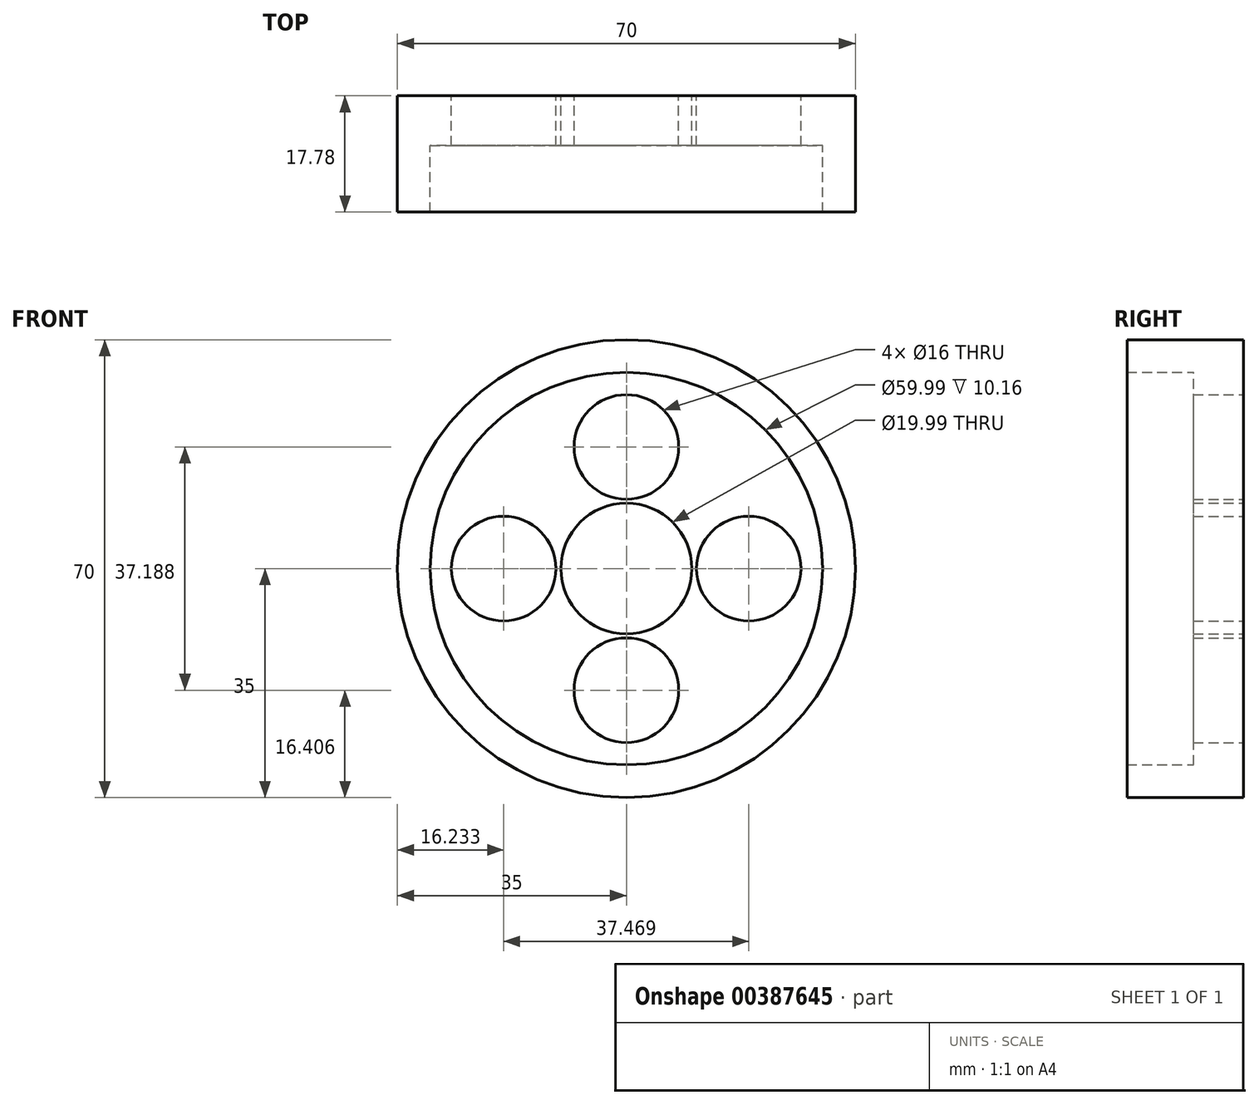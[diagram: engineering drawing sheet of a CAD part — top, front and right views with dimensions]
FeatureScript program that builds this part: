
annotation { "Feature Type Name" : "Feature", "Feature Type Description" : "" }
export const myFeature = defineFeature(function(context is Context, id is Id, definition is map)
    precondition{}
    {
        {
            var Q0;
            Q0=qCreatedBy(makeId("Front.planeOp"),FACE);
            var sketch = newSketch(context, id + "F0", { "sketchPlane" : qUnion([Q0])});
            skCircle(sketch, "E0", {"center": v(0, 0) * mm, "radius": 35 * mm});
            skCircle(sketch, "E1", {"center": v(0, 0) * mm, "radius": 30 * mm});
            skCircle(sketch, "E2", {"center": v(0, 0) * mm, "radius": 10 * mm});
            skCircle(sketch, "E3", {"center": v(0, 18.6) * mm, "radius": 8 * mm});
            skCircle(sketch, "E4", {"center": v(18.7, 0) * mm, "radius": 8 * mm});
            skCircle(sketch, "E5", {"center": v(0, -18.6) * mm, "radius": 8 * mm});
            skCircle(sketch, "E6", {"center": v(-18.77, 0) * mm, "radius": 8 * mm});
            skCircle(sketch, "E7", {"center": v(0, 0) * mm, "radius": 7.16 * mm});
            skSolve(sketch);
        }
        {
            var Q0;
            Q0=makeQuery(id+"F0.imprint","IMPRINT",FACE,{"disambiguationData":[TD([[makeQuery(id+"F0.imprint","IMPRINT",EDGE,{"derivedFrom":sQuery(id+"F0.wireOp",EDGE,"E0")}),1.0]])]});
            extrude(context, id + "F1", {"entities" : qUnion([Q0]), "depth" : 15.24 * mm});
        }
        {
            var Q0;
            Q0 = qSketchRegion(id + "F0", true);
            extrude(context, id + "F2", {"entities" : qUnion([Q0]), "operationType" : NewBodyOperationType.ADD, "depth" : 17.78 * mm});
        }
        {
            var Q0;
            Q0=makeQuery(id+"F0.imprint","IMPRINT",FACE,{"disambiguationData":[TD([[makeQuery(id+"F0.imprint","IMPRINT",EDGE,{"derivedFrom":sQuery(id+"F0.wireOp",EDGE,"E1")}),1.0]])]});
            extrude(context, id + "F3", {"entities" : qUnion([Q0]), "operationType" : NewBodyOperationType.ADD, "depth" : 7.62 * mm});
        }
        {
            var Q0;
            Q0=sQuery(id+"F0.wireOp",EDGE,"E2");
            extrude(context, id + "F4", {"bodyType" : ToolBodyType.SURFACE, "surfaceEntities" : qUnion([Q0]), "depth" : 20.32 * mm});
        }
    });
